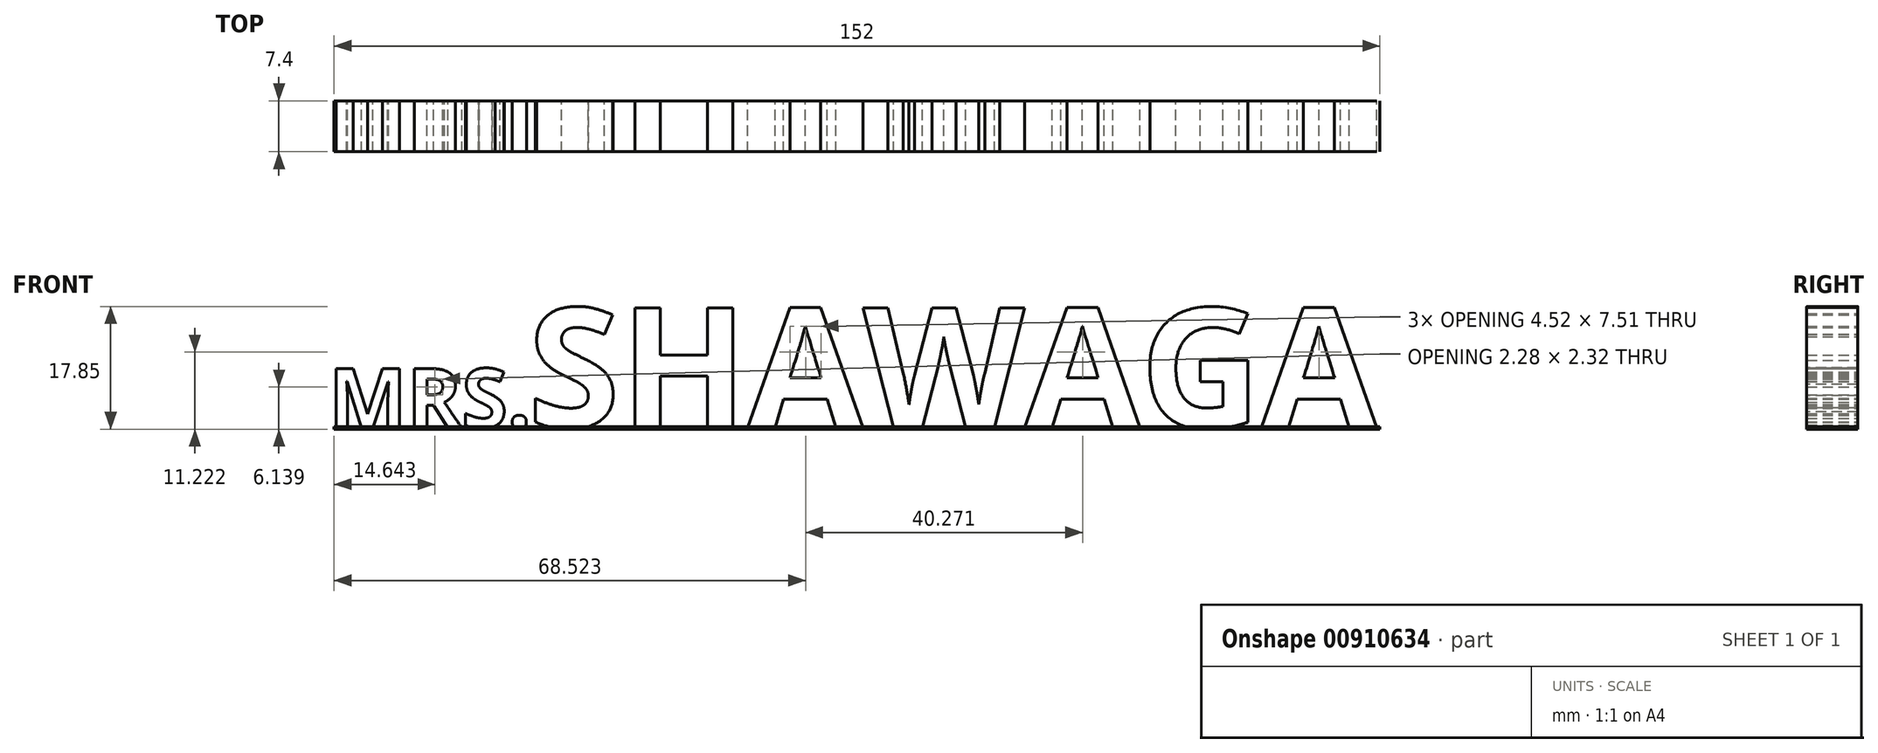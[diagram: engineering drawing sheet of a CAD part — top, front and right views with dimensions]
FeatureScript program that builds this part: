
annotation { "Feature Type Name" : "Feature", "Feature Type Description" : "" }
export const myFeature = defineFeature(function(context is Context, id is Id, definition is map)
    precondition{}
    {
        {
            var Q0;
            Q0=qCreatedBy(makeId("Front.planeOp"),FACE);
            var sketch = newSketch(context, id + "F0", { "sketchPlane" : qUnion([Q0])});
            skText(sketch, "E0", { "text": "SHAWAGA", "fontName": "OpenSans-Bold.ttf"});
            const initialGuessF0  = {"E0": [-0.0196, -0.00612, 1, 0, 0.0175]};
            skSetInitialGuess(sketch, initialGuessF0);
            skSolve(sketch);
        }
        {
            var Q0;
            Q0=qCreatedBy(makeId("Front.planeOp"),FACE);
            var sketch = newSketch(context, id + "F1", { "sketchPlane" : qUnion([Q0])});
            skText(sketch, "E1", { "text": "MRS.", "fontName": "OpenSans-Bold.ttf"});
            const initialGuessF1  = {"E1": [-0.0485, -0.00618, 1, 0, 0.00868]};
            skSetInitialGuess(sketch, initialGuessF1);
            skSolve(sketch);
        }
        {
            var Q0;
            Q0=qCreatedBy(makeId("Front.planeOp"),FACE);
            var sketch = newSketch(context, id + "F2", { "sketchPlane" : qUnion([Q0])});
            skLineSegment(sketch, "E2.bottom", {"start": v(-47.73, -5.98) * mm, "end": v(104.27, -5.98) * mm});
            skLineSegment(sketch, "E2.top", {"start": v(-47.73, -6.37) * mm, "end": v(104.27, -6.37) * mm});
            skLineSegment(sketch, "E2.left", {"start": v(-47.73, -5.98) * mm, "end": v(-47.73, -6.37) * mm});
            skLineSegment(sketch, "E2.right", {"start": v(104.27, -5.98) * mm, "end": v(104.27, -6.37) * mm});
            skSolve(sketch);
        }
        {
            var Q0;
            Q0 = qSketchRegion(id + "F0", true);
            extrude(context, id + "F3", {"entities" : qUnion([Q0]), "depth" : 7.4 * mm, "offsetDistance" : 25 * mm});
        }
        {
            var Q0;
            Q0 = qSketchRegion(id + "F1", true);
            extrude(context, id + "F4", {"entities" : qUnion([Q0]), "depth" : 7.4 * mm, "offsetDistance" : 25 * mm});
        }
        {
            var Q0;
            Q0 = qSketchRegion(id + "F2", true);
            extrude(context, id + "F5", {"entities" : qUnion([Q0]), "depth" : 7.4 * mm, "offsetDistance" : 25 * mm});
        }
    });
